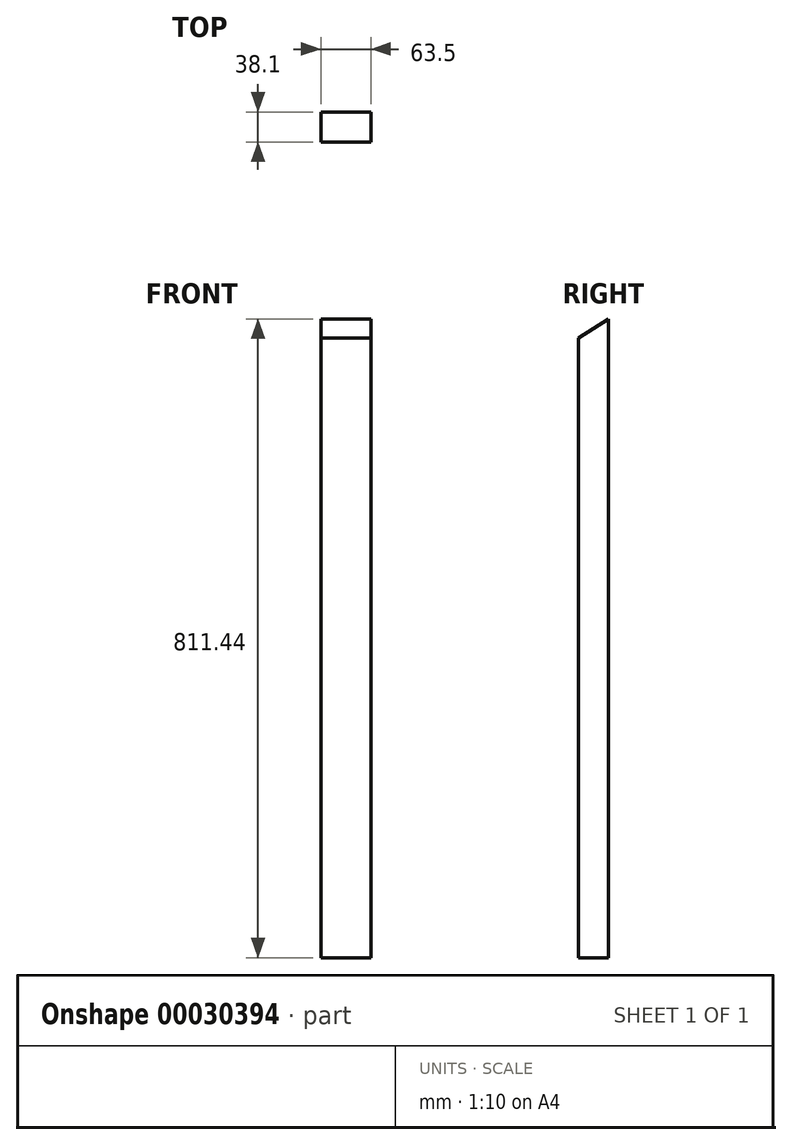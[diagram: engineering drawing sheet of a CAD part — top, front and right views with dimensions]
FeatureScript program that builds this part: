
annotation { "Feature Type Name" : "Feature", "Feature Type Description" : "" }
export const myFeature = defineFeature(function(context is Context, id is Id, definition is map)
    precondition{}
    {
        {
            var Q0;
            Q0=qCreatedBy(makeId("Right.planeOp"),FACE);
            var sketch = newSketch(context, id + "F0", { "sketchPlane" : qUnion([Q0])});
            skLineSegment(sketch, "E0", {"start": v(0, 405.72) * mm, "end": v(-38.1, 381.68) * mm});
            skLineSegment(sketch, "E1", {"start": v(-38.1, 381.68) * mm, "end": v(-38.1, -405.72) * mm});
            skLineSegment(sketch, "E2", {"start": v(-38.1, -405.72) * mm, "end": v(0, -405.72) * mm});
            skLineSegment(sketch, "E3", {"start": v(0, -405.72) * mm, "end": v(0, 405.72) * mm});
            skSolve(sketch);
        }
        {
            var Q0;
            Q0=makeQuery(id+"F0.imprint","IMPRINT",FACE,{"disambiguationData":[TD([[makeQuery(id+"F0.imprint","IMPRINT",EDGE,{"derivedFrom":sQuery(id+"F0.wireOp",EDGE,"E0")}),1.0]])]});
            extrude(context, id + "F1", {"entities" : qUnion([Q0]), "endBound" : BoundingType.SYMMETRIC, "depth" : 63.5 * mm});
        }
    });
